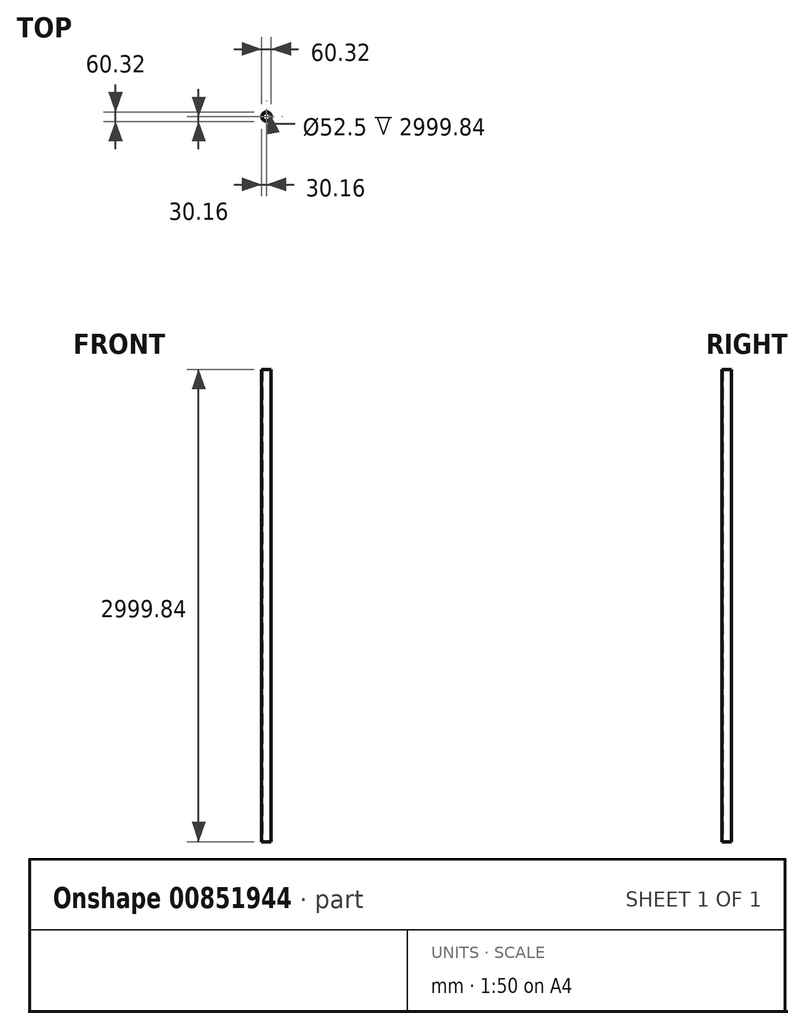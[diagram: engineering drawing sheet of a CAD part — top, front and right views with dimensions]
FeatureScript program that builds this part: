
annotation { "Feature Type Name" : "Feature", "Feature Type Description" : "" }
export const myFeature = defineFeature(function(context is Context, id is Id, definition is map)
    precondition{}
    {
        {
            var Q0;
            Q0=qCreatedBy(makeId("Top.planeOp"),FACE);
            var sketch = newSketch(context, id + "F0", { "sketchPlane" : qUnion([Q0])});
            skCircle(sketch, "E0", {"center": v(0, 0) * mm, "radius": 30.16 * mm});
            skCircle(sketch, "E1", {"center": v(0, 0) * mm, "radius": 26.25 * mm});
            skSolve(sketch);
        }
        {
            var Q0;
            Q0=qSketchRegion(id+"F0",true);
            extrude(context, id + "F1", {"entities" : qUnion([Q0]), "depth" : 2999.84 * mm, "offsetDistance" : 25.4 * mm});
        }
    });
